# Revit family: VIESSMANN - Vitocrossal 200 CM2
name_source: partatom
category: Wyposażenie mechaniczne
revit_build: Autodesk Revit 2017 (Build: 20160720_1515(x64)
units: mm (PartAtom-declared; Revit-internal decimal feet)

## family parameters
Numer OmniClass = 23.15.30.27.21
Oparty na płaszczyźnie roboczej = Nie
Punkt obliczania pomieszczeń = Nie
Tnij formami wycięć po wczytaniu = Tak
Typ części = Normalny
Tytuł OmniClass = Gas Tanks and Gasholders
Współdzielony = Nie
Wymiar okrągłego złącza = Użyj średnicy
Zawsze pionowo = Tak

## types (3) — shared parameters
Autor = https://www.archispace.pl
Ciśnienie kontrolne = 0.8 MPa
Ciśnienie na przyłączu gazu płynnego = 0.0 MPa
Ciśnienie na przyłączu gazu ziemnego = 0.0 MPa
Częstotliwość = 50 Hz
Dop. ciśnienie robocze = 0.6 MPa
Dop. temperatura na zasilaniu (=temperatura progowa) = 110 °C
Dop. temperatura robocza = 95 °C
Długość palnika = 506 mm  [stored 1.6601 ft]
Liczba biegunów = 1
Maks. ciśnienie na przyłączu gazu płynnego = 0.0 MPa
Maks. ciśnienie na przyłączu gazu ziemnego = 0.0 MPa
Mufa R1/2 do dodatkowych regulatorów = 1/2"
Napięcie zasilania = 230 V
Numer identyfikacyjny produktu = CE-0085BQ0021
Odsunięcie spustu = 155 mm  [stored 0.50853 ft]
Opis = Gazowy kocioł grzewczy
Opis indeksowy = CE-0085BQ0021
Opory przepływu = 0.0 MPa
PN 6 DN - powrót do kotła = 100 mm  [stored 0.328084 ft]
PN 6 DN - zasilanie z kotła = 100 mm  [stored 0.328084 ft]
Parametry spalin - dyspozycyjne ciśnienie tłoczenia na króćcu spalin = 0.0 MPa
Parametry spalin - przy obciążeniu częściowym (przy temp. wody na powrocie wyn. 30°C) = 35 °C
Parametry spalin - przy obciążeniu częściowym (przy temp. wody na powrocie wyn. 60°C) = 60 °C
Parametry spalin - przy znamionowej mocy cieplnej (przy temp. wody na powrocie wyn. 30°C) = 45 °C
Parametry spalin - przy znamionowej mocy cieplnej (przy temp. wody na powrocie wyn. 60°C) = 75 °C
Poziom ciśnienia akustycznego - 1m przed kotłem (obciążenie pełne) = 67 dB(A)
Producent = Viessmann Sp.z.o.o.
Przyłącze spalin = 250 mm  [stored 0.82021 ft]
Sprawność znormalizowana przy temperaturze w systemie grzewczym wyn. 50/30°C = do 98 (Hs) %
Sprawność znormalizowana przy temperaturze w systemie grzewczym wyn. 75/60°C = do 95 (Hs) %
Spust = 1"
Straty energii dyżurnej qB,70 = 0.3 %
Syfon z odpływem kondensatu = 20.00 mm
Typ palnika = CM2 - cylindryczny MatriX
URL = https://www.viessmann-projektant.pl
Viessmann Kolor 1 = Viessmann Kolor 1
Viessmann Kolor 2 = Viessmann Kolor 2
Viessmann Kolor 3 = Viessmann Kolor 3
Współczynnik mocy = 1
Wykonanie palnika = Wbudowany Modulowany
Wysokość fundamentu = 100 mm  [stored 0.328084 ft]
Zawór bezpieczeństwa (gwint zewnętrzny) = 1 1/4"

## per-type parameters (varying)
- CM2 500kW: Długośc podstawy=1345 mm; Długość=2385 mm; Długość całkowita=2385 mm; Długość całkowita palnika=990 mm  [stored 3.24803 ft]; Długość fundamentu=1450 mm  [stored 4.75722 ft]; Długość korpusu=2320 mm; Masa - korpus kotła=512.00 kg; Masa - palnik z armaturą uniwersalną i pokrywą palnika=41.00 kg; Masa całkowita=687.00 kg; Moc cieplna palnika dolna=95 kW; Moc cieplna palnika górna=474 kW; Moc nominalna=500 kW; Model=Gazowy kocioł kondensacyjny Viessmann Vitocrossal 200 CM2 500kW / Gas condensing boiler Viessmann Vitocrossal 200 CM2 500kW; Odsunięcie RG=435 mm  [stored 1.42717 ft]; Odsunięcie króćca zasilania=870 mm  [stored 2.85433 ft]; Odsunięcie powrotu do kotła=370 mm  [stored 1.21391 ft]; Odsunięcie przyłącza zabezpieczającego=310 mm  [stored 1.01706 ft]; Parametry spalin - masowe natężenie przepływu w przypadku gazu ziemnego przy obciążeniu częściowym=144 kg/h; Parametry spalin - masowe natężenie przepływu w przypadku gazu ziemnego przy znamionowej mocy cieplnej=720 kg/h; Pobór mocy elektrycznej - przy dolnej mocy cieplnej=66 W; Pobór mocy elektrycznej - przy górnej mocy cieplnej=655 W; Pojemność wodna kotła=430.0 L; Poziom ciśnienia akustycznego - w rurze spalin (obciążenie pełne)=107 dB(A); Przepływ maksymalny=21.60 m³/h; Przyłącze gazu=1 1/2"; Szerokośc korpusu=1080 mm  [stored 3.54331 ft]; Szerokość=1245 mm; Szerokość całkowita=1245 mm; Szerokość fundamentu=1050 mm; Szerokość palnika=620 mm  [stored 2.03412 ft]; Szerokość podstawy=910 mm; Wartości na przyłączu (w odniesieniu do maks. obciążenia) - gaz płynny P/G31=9.2 do 36.8 kg/h; Wartości na przyłączu (w odniesieniu do maks. obciążenia) - gaz ziemny GZ-50/G20=10.0 do 50.2 m3/h; Wartości na przyłączu (w odniesieniu do maks. obciążenia) - gaz ziemny GZ41,5/G27=11.7 do 58.3 m3/h; Wysokośc korpusu=1370 mm; Wysokośc króćców przyłączeniowych=1510 mm; Wysokość=1510 mm; Wysokość palnika=622 mm  [stored 2.04068 ft]; Wysokość przyłącza spalin=710 mm; Zakres znamionowej mocy cieplnej przy Tv/Tr 50/30°C - gaz płynny=125 do 500 kW; Zakres znamionowej mocy cieplnej przy Tv/Tr 50/30°C - gaz ziemny=100 do 500 kW; Zakres znamionowej mocy cieplnej przy Tv/Tr 80/60°C - gaz płynny=115 do 460 kW; Zakres znamionowej mocy cieplnej przy Tv/Tr 80/60°C - gaz ziemny=92 do 460 kW; Znamionowe obciążenie cieplne - gaz płynny=119 do 474 kW; Znamionowe obciążenie cieplne - gaz ziemny=95 do 474 kW; odsuniecie wyswietlacza=1160 mm  [stored 3.80577 ft]
- CM2 620kW: Długośc podstawy=1475 mm  [stored 4.83924 ft]; Długość=2525 mm; Długość całkowita=2525 mm; Długość całkowita palnika=1070 mm  [stored 3.5105 ft]; Długość fundamentu=1600 mm; Długość korpusu=2455 mm; Masa - korpus kotła=581.00 kg; Masa - palnik z armaturą uniwersalną i pokrywą palnika=42.00 kg; Masa całkowita=758.00 kg; Moc cieplna palnika dolna=119 kW; Moc cieplna palnika górna=593 kW; Moc nominalna=620 kW; Model=Gazowy kocioł kondensacyjny Viessmann Vitocrossal 200 CM2 620kW / Gas condensing boiler Viessmann Vitocrossal 200 CM2 620kW; Odsunięcie RG=480 mm  [stored 1.5748 ft]; Odsunięcie króćca zasilania=880 mm  [stored 2.88714 ft]; Odsunięcie powrotu do kotła=415 mm  [stored 1.36155 ft]; Odsunięcie przyłącza zabezpieczającego=350 mm  [stored 1.14829 ft]; Parametry spalin - masowe natężenie przepływu w przypadku gazu ziemnego przy obciążeniu częściowym=181 kg/h; Parametry spalin - masowe natężenie przepływu w przypadku gazu ziemnego przy znamionowej mocy cieplnej=901 kg/h; Pobór mocy elektrycznej - przy dolnej mocy cieplnej=74 W; Pobór mocy elektrycznej - przy górnej mocy cieplnej=835 W; Pojemność wodna kotła=503.0 L; Poziom ciśnienia akustycznego - w rurze spalin (obciążenie pełne)=109 dB(A); Przepływ maksymalny=26.78 m³/h; Przyłącze gazu=1 1/2"; Szerokośc korpusu=1130 mm  [stored 3.70735 ft]; Szerokość=1295 mm; Szerokość całkowita=1295 mm; Szerokość fundamentu=1100 mm; Szerokość palnika=620 mm  [stored 2.03412 ft]; Szerokość podstawy=960 mm  [stored 3.14961 ft]; Wartości na przyłączu (w odniesieniu do maks. obciążenia) - gaz płynny P/G31=11.5 do 46.1 kg/h; Wartości na przyłączu (w odniesieniu do maks. obciążenia) - gaz ziemny GZ-50/G20=12.5 do 62.7 m3/h; Wartości na przyłączu (w odniesieniu do maks. obciążenia) - gaz ziemny GZ41,5/G27=14.6 do 72.9 m3/h; Wysokośc korpusu=1510 mm; Wysokośc króćców przyłączeniowych=1620 mm; Wysokość=1580 mm; Wysokość palnika=622 mm  [stored 2.04068 ft]; Wysokość przyłącza spalin=735 mm; Zakres znamionowej mocy cieplnej przy Tv/Tr 50/30°C - gaz płynny=155 do 620 kW; Zakres znamionowej mocy cieplnej przy Tv/Tr 50/30°C - gaz ziemny=124 do 620 kW; Zakres znamionowej mocy cieplnej przy Tv/Tr 80/60°C - gaz płynny=144 do 575 kW; Zakres znamionowej mocy cieplnej przy Tv/Tr 80/60°C - gaz ziemny=115 do 575 kW; Znamionowe obciążenie cieplne - gaz płynny=148 do 593 kW; Znamionowe obciążenie cieplne - gaz ziemny=119 do 593 kW; odsuniecie wyswietlacza=1228 mm
- CM2 400kW: Długośc podstawy=1185 mm  [stored 3.8878 ft]; Długość=2230 mm; Długość całkowita=2230 mm; Długość całkowita palnika=990 mm  [stored 3.24803 ft]; Długość fundamentu=1300 mm  [stored 4.26509 ft]; Długość korpusu=2165 mm; Masa - korpus kotła=446.00 kg; Masa - palnik z armaturą uniwersalną i pokrywą palnika=34.00 kg; Masa całkowita=597.00 kg; Moc cieplna palnika dolna=76 kW; Moc cieplna palnika górna=381 kW; Moc nominalna=400 kW; Model=Gazowy kocioł kondensacyjny Viessmann Vitocrossal 200 CM2 400kW / Gas condensing boiler Viessmann Vitocrossal 200 CM2 400kW; Odsunięcie RG=385 mm  [stored 1.26312 ft]; Odsunięcie króćca zasilania=870 mm  [stored 2.85433 ft]; Odsunięcie powrotu do kotła=320 mm  [stored 1.04987 ft]; Odsunięcie przyłącza zabezpieczającego=255 mm  [stored 0.836614 ft]; Parametry spalin - masowe natężenie przepływu w przypadku gazu ziemnego przy obciążeniu częściowym=116 kg/h; Parametry spalin - masowe natężenie przepływu w przypadku gazu ziemnego przy znamionowej mocy cieplnej=579 kg/h; Pobór mocy elektrycznej - przy dolnej mocy cieplnej=69 W; Pobór mocy elektrycznej - przy górnej mocy cieplnej=576 W; Pojemność wodna kotła=402.0 L; Poziom ciśnienia akustycznego - w rurze spalin (obciążenie pełne)=114 dB(A); Przepływ maksymalny=17.28 m³/h; Przyłącze gazu=1 1/4"; Szerokośc korpusu=1080 mm  [stored 3.54331 ft]; Szerokość=1245 mm; Szerokość całkowita=1245 mm; Szerokość fundamentu=1050 mm; Szerokość palnika=565 mm  [stored 1.85367 ft]; Szerokość podstawy=910 mm; Wartości na przyłączu (w odniesieniu do maks. obciążenia) - gaz płynny P/G31=7.4 do 29.6 kg/h; Wartości na przyłączu (w odniesieniu do maks. obciążenia) - gaz ziemny GZ-50/G20=8.1 do 40.4 m3/h; Wartości na przyłączu (w odniesieniu do maks. obciążenia) - gaz ziemny GZ41,5/G27=9.4 do 46.9 m3/h; Wysokośc korpusu=1370 mm; Wysokośc króćców przyłączeniowych=1480 mm; Wysokość=1480 mm; Wysokość palnika=540 mm  [stored 1.77165 ft]; Wysokość przyłącza spalin=710 mm; Zakres znamionowej mocy cieplnej przy Tv/Tr 50/30°C - gaz płynny=100 do 400 kW; Zakres znamionowej mocy cieplnej przy Tv/Tr 50/30°C - gaz ziemny=80 do 400 kW; Zakres znamionowej mocy cieplnej przy Tv/Tr 80/60°C - gaz płynny=93 do 370 kW; Zakres znamionowej mocy cieplnej przy Tv/Tr 80/60°C - gaz ziemny=74 do 370 kW; Znamionowe obciążenie cieplne - gaz płynny=95 do 381 kW; Znamionowe obciążenie cieplne - gaz ziemny=76 do 381 kW; odsuniecie wyswietlacza=1083 mm

note: [stored X ft] marks values corroborated as IEEE doubles in the binary element streams (Revit-internal decimal feet)
